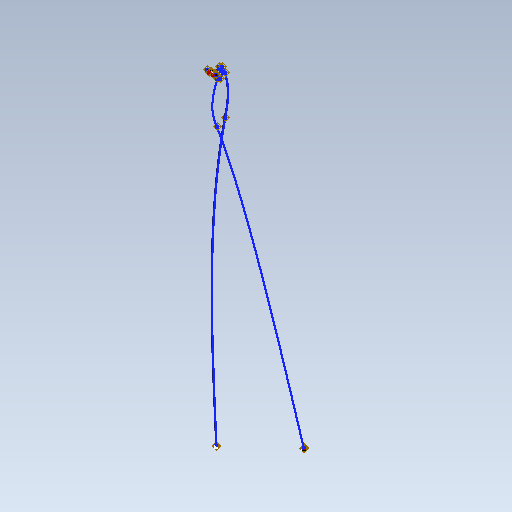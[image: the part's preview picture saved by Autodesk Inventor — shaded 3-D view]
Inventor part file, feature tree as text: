
AUTODESK INVENTOR PART (.ipt)
format: ipt  version: 2020 (Build 240168000, 168)  size: 188,928 bytes
history: native  units: mm (DEFAULTED — no unit token found)
features: other x49, plane x2, sketch x2
bodies: Body1 (feature_tree)
feature tree (53):
  other  "Origen"
  other  "Punto de trabajo1"
  other  "Punto de trabajo2"
  other  "Segmento1"
  other  "Punto de trabajo3"
  other  "Punto de trabajo4"
  other  "Punto de trabajo5"
  other  "Punto de trabajo6"
  plane  "Plano de trabajo1"
  other  "Punto de trabajo7"
  other  "Punto de trabajo8"
  other  "Segmento2"
  other  "Punto de trabajo9"
  other  "Punto de trabajo10"
  other  "Punto de trabajo11"
  other  "Punto de trabajo12"
  plane  "Plano de trabajo2"
  other  "Punto de trabajo13"
  other  "Punto de trabajo14"
  other  "Cable1:1"
  other  "Punto de trabajo15"
  other  "Punto de trabajo16"
  other  "Cable1:2"
  other  "Punto de trabajo17"
  other  "Punto de trabajo18"
  other  "Cable1:3"
  other  "Punto de trabajo19"
  other  "Punto de trabajo20"
  other  "Cable1:4"
  other  "Punto de trabajo21"
  other  "Punto de trabajo22"
  other  "Cable2:1"
  other  "Punto de trabajo23"
  other  "Punto de trabajo24"
  other  "Cable2:2"
  other  "Punto de trabajo25"
  other  "Punto de trabajo26"
  other  "Cable2:3"
  other  "Punto de trabajo27"
  other  "Punto de trabajo28"
  other  "Cable2:4"
  other  "Plano YZ"
  other  "Plano XZ"
  other  "Plano XY"
  other  "Eje X"
  other  "Eje Y"
  other  "Eje Z"
  sketch  "Boceto1"  dims[d0=0.0mm d1=0.0mm]
  other  "Sup1"
  sketch  "Boceto2"  dims[d2=0.0mm d3=0.0mm]
  other  "Sup2"
  other  "SuperficieBarrido1"
  other  "SuperficieBarrido2"
